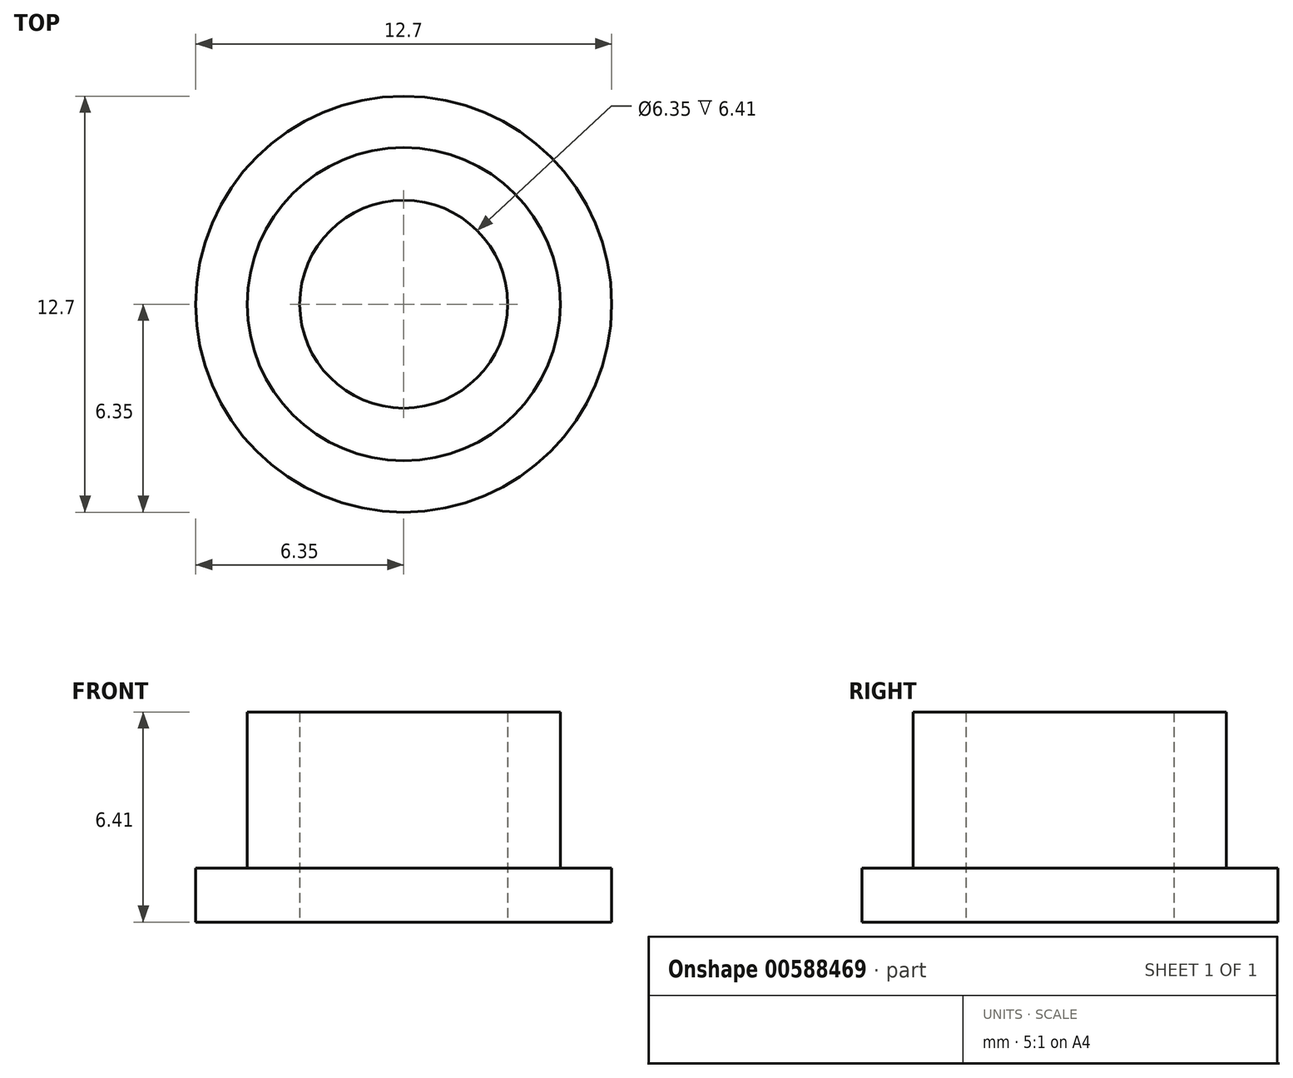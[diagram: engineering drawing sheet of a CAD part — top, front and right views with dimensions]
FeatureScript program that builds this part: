
annotation { "Feature Type Name" : "Feature", "Feature Type Description" : "" }
export const myFeature = defineFeature(function(context is Context, id is Id, definition is map)
    precondition{}
    {
        {
            var Q0;
            Q0=qCreatedBy(makeId("Top.planeOp"),FACE);
            var sketch = newSketch(context, id + "F0", { "sketchPlane" : qUnion([Q0])});
            skCircle(sketch, "E0", {"center": v(0, 0) * mm, "radius": 4.78 * mm});
            skCircle(sketch, "E1", {"center": v(0, 0) * mm, "radius": 3.17 * mm});
            skCircle(sketch, "E2", {"center": v(0, 0) * mm, "radius": 6.35 * mm});
            skSolve(sketch);
        }
        {
            var Q0;
            Q0=makeQuery(id+"F0.imprint","IMPRINT",FACE,{"disambiguationData":[TD([[makeQuery(id+"F0.imprint","IMPRINT",EDGE,{"derivedFrom":sQuery(id+"F0.wireOp",EDGE,"E0")}),1.0]])]});
            extrude(context, id + "F1", {"entities" : qUnion([Q0]), "depth" : 6.33 * mm, "offsetDistance" : 25 * mm});
        }
        {
            var Q0;
            Q0=makeQuery(id+"F0.imprint","IMPRINT",FACE,{"disambiguationData":[TD([[makeQuery(id+"F0.imprint","IMPRINT",EDGE,{"derivedFrom":sQuery(id+"F0.wireOp",EDGE,"E0")}),1.0]])]});
            extrude(context, id + "F2", {"entities" : qUnion([Q0]), "depth" : 6.4 * mm, "offsetDistance" : 25 * mm});
        }
        {
            var Q0;
            Q0 = qSketchRegion(id + "F0", true);
            extrude(context, id + "F3", {"entities" : qUnion([Q0]), "operationType" : NewBodyOperationType.ADD, "depth" : 1.65 * mm, "offsetDistance" : 25 * mm});
        }
    });
